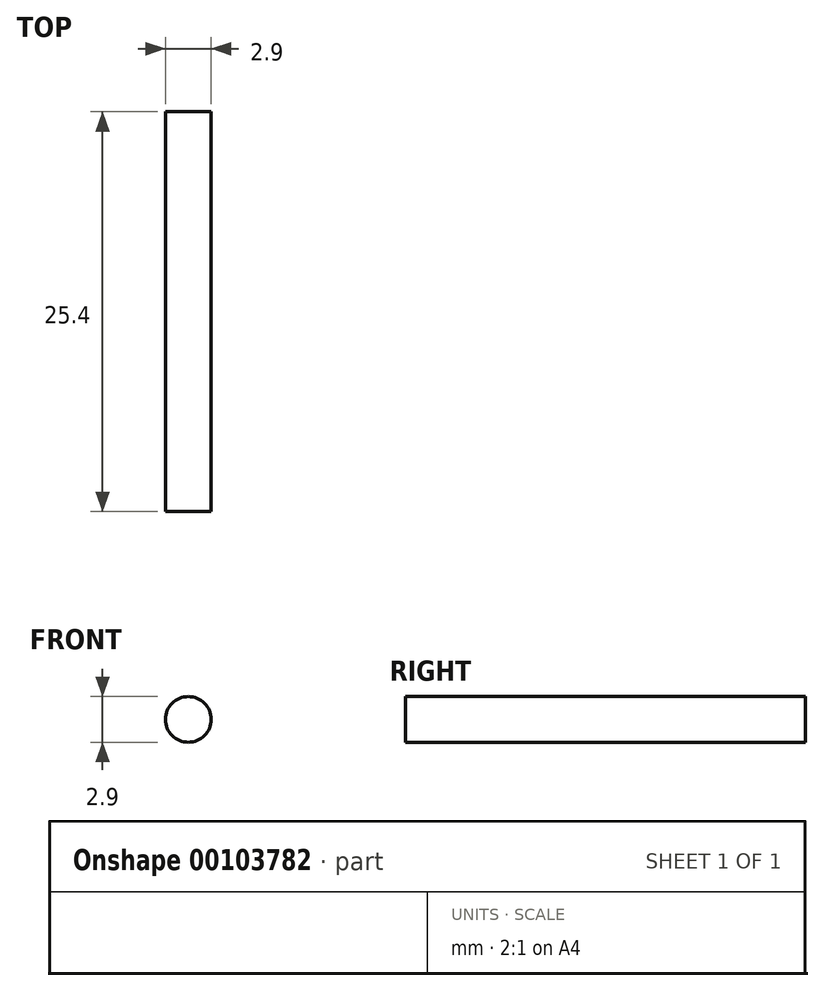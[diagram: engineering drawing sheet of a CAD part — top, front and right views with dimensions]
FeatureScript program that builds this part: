
annotation { "Feature Type Name" : "Feature", "Feature Type Description" : "" }
export const myFeature = defineFeature(function(context is Context, id is Id, definition is map)
    precondition{}
    {
        {
            var Q0;
            Q0=qCreatedBy(makeId("Front.planeOp"),FACE);
            var sketch = newSketch(context, id + "F0", { "sketchPlane" : qUnion([Q0])});
            skCircle(sketch, "E0", {"center": v(0, 0) * mm, "radius": 1.45 * mm});
            skSolve(sketch);
        }
        {
            var Q0;
            Q0=makeQuery(id+"F0.imprint","IMPRINT",FACE,{"disambiguationData":[TD([[makeQuery(id+"F0.imprint","IMPRINT",EDGE,{"derivedFrom":sQuery(id+"F0.wireOp",EDGE,"E0")}),1.0]])]});
            extrude(context, id + "F1", {"entities" : qUnion([Q0]), "depth" : 25.4 * mm});
        }
    });
